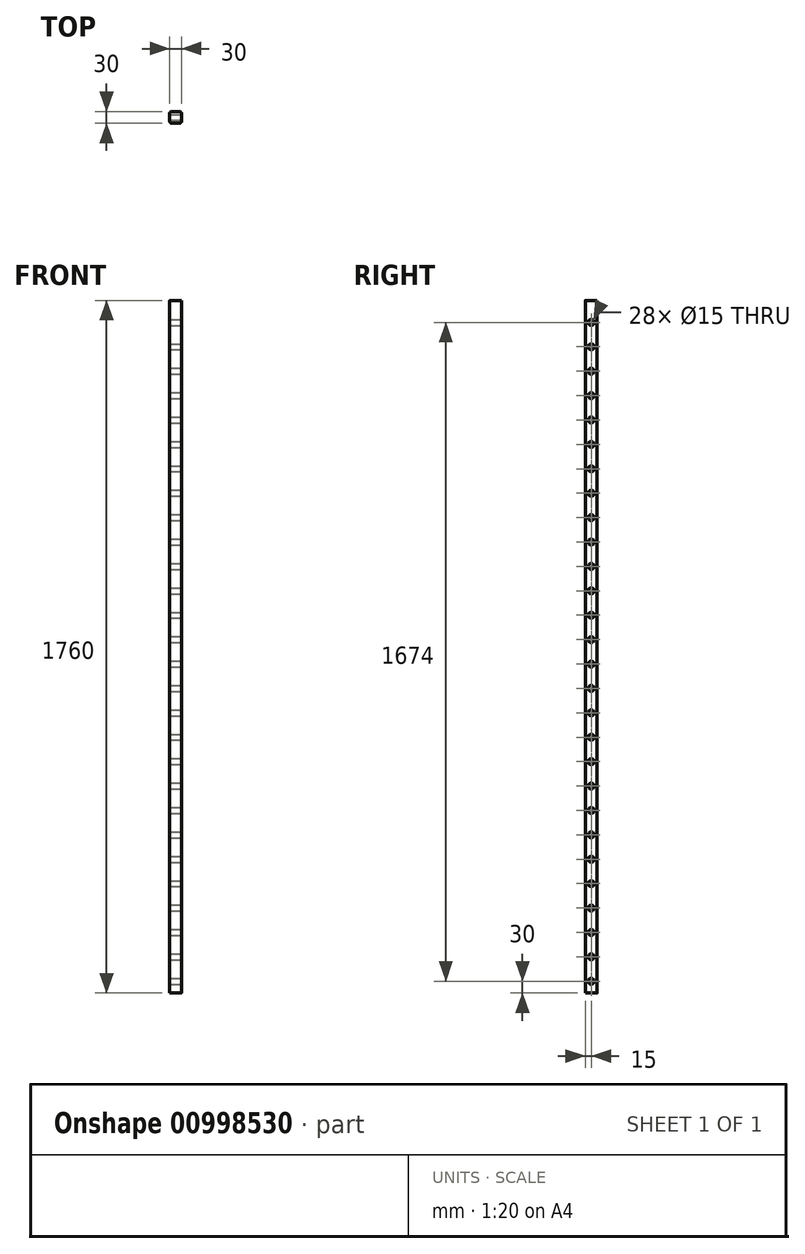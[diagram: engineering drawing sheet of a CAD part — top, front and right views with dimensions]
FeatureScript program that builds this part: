
annotation { "Feature Type Name" : "Feature", "Feature Type Description" : "" }
export const myFeature = defineFeature(function(context is Context, id is Id, definition is map)
    precondition{}
    {
        {
            var Q0;
            Q0=qCreatedBy(makeId("Top.planeOp"),FACE);
            var sketch = newSketch(context, id + "F0", { "sketchPlane" : qUnion([Q0])});
            skLineSegment(sketch, "E0.bottom", {"start": v(15, -15) * mm, "end": v(-15, -15) * mm});
            skLineSegment(sketch, "E0.top", {"start": v(15, 15) * mm, "end": v(-15, 15) * mm});
            skLineSegment(sketch, "E0.left", {"start": v(15, -15) * mm, "end": v(15, 15) * mm});
            skLineSegment(sketch, "E0.right", {"start": v(-15, -15) * mm, "end": v(-15, 15) * mm});
            skPoint(sketch, "E0.middle", {"position": v(0, 0) * mm});
            skSolve(sketch);
        }
        {
            var Q0;
            Q0 = qSketchRegion(id + "F0", true);
            extrude(context, id + "F1", {"entities" : qUnion([Q0]), "depth" : 1760 * mm, "offsetDistance" : 25 * mm});
        }
        {
            var Q0;
            Q0=makeQuery(id+"F1.opExtrude","SWEPT_FACE",FACE,{"disambiguationData":[OSD([sQuery(id+"F0.wireOp",EDGE,"E0.left")])]});
            var sketch = newSketch(context, id + "F2", { "sketchPlane" : qUnion([Q0])});
            skCircle(sketch, "E1", {"center": v(0, 30) * mm, "radius": 7.5 * mm});
            skCircle(sketch, "E2.0.1.0", {"center": v(0, 92) * mm, "radius": 7.5 * mm});
            skCircle(sketch, "E2.0.2.0", {"center": v(0, 154) * mm, "radius": 7.5 * mm});
            skCircle(sketch, "E2.0.3.0", {"center": v(0, 216) * mm, "radius": 7.5 * mm});
            skCircle(sketch, "E2.0.4.0", {"center": v(0, 278) * mm, "radius": 7.5 * mm});
            skCircle(sketch, "E2.0.5.0", {"center": v(0, 340) * mm, "radius": 7.5 * mm});
            skCircle(sketch, "E2.0.6.0", {"center": v(0, 402) * mm, "radius": 7.5 * mm});
            skCircle(sketch, "E2.0.7.0", {"center": v(0, 464) * mm, "radius": 7.5 * mm});
            skCircle(sketch, "E2.0.8.0", {"center": v(0, 526) * mm, "radius": 7.5 * mm});
            skCircle(sketch, "E2.0.9.0", {"center": v(0, 588) * mm, "radius": 7.5 * mm});
            skCircle(sketch, "E2.0.10.0", {"center": v(0, 650) * mm, "radius": 7.5 * mm});
            skCircle(sketch, "E2.0.11.0", {"center": v(0, 712) * mm, "radius": 7.5 * mm});
            skCircle(sketch, "E2.0.12.0", {"center": v(0, 774) * mm, "radius": 7.5 * mm});
            skCircle(sketch, "E2.0.13.0", {"center": v(0, 836) * mm, "radius": 7.5 * mm});
            skCircle(sketch, "E2.0.14.0", {"center": v(0, 898) * mm, "radius": 7.5 * mm});
            skCircle(sketch, "E2.0.15.0", {"center": v(0, 960) * mm, "radius": 7.5 * mm});
            skCircle(sketch, "E2.0.16.0", {"center": v(0, 1022) * mm, "radius": 7.5 * mm});
            skCircle(sketch, "E2.0.17.0", {"center": v(0, 1084) * mm, "radius": 7.5 * mm});
            skCircle(sketch, "E2.0.18.0", {"center": v(0, 1146) * mm, "radius": 7.5 * mm});
            skCircle(sketch, "E2.0.19.0", {"center": v(0, 1208) * mm, "radius": 7.5 * mm});
            skCircle(sketch, "E2.0.20.0", {"center": v(0, 1270) * mm, "radius": 7.5 * mm});
            skCircle(sketch, "E2.0.21.0", {"center": v(0, 1332) * mm, "radius": 7.5 * mm});
            skCircle(sketch, "E2.0.22.0", {"center": v(0, 1394) * mm, "radius": 7.5 * mm});
            skCircle(sketch, "E2.0.23.0", {"center": v(0, 1456) * mm, "radius": 7.5 * mm});
            skCircle(sketch, "E2.0.24.0", {"center": v(0, 1518) * mm, "radius": 7.5 * mm});
            skCircle(sketch, "E2.0.25.0", {"center": v(0, 1580) * mm, "radius": 7.5 * mm});
            skCircle(sketch, "E2.0.26.0", {"center": v(0, 1642) * mm, "radius": 7.5 * mm});
            skCircle(sketch, "E2.0.27.0", {"center": v(0, 1704) * mm, "radius": 7.5 * mm});
            skLineSegment(sketch, "E2.direction1", {"start": v(0, 30) * mm, "end": v(25, 30) * mm, "construction": true});
            skLineSegment(sketch, "E2.direction2", {"start": v(0, 30) * mm, "end": v(0, 92) * mm, "construction": true});
            skSolve(sketch);
        }
        {
            var Q0;
            Q0 = qSketchRegion(id + "F2", true);
            extrude(context, id + "F3", {"entities" : qUnion([Q0]), "operationType" : NewBodyOperationType.REMOVE, "endBound" : BoundingType.THROUGH_ALL, "oppositeDirection" : true, "depth" : 25 * mm, "offsetDistance" : 25 * mm});
        }
        {
            var Q0;
            Q0=makeQuery(id+"F1.opExtrude","SWEPT_EDGE",EDGE,{"disambiguationData":[OSD([sQuery(id+"F0.wireOp",EDGE,"E0.bottom"),sQuery(id+"F0.wireOp",EDGE,"E0.left")])]});
            var Q1;
            Q1=makeQuery(id+"F1.opExtrude","SWEPT_EDGE",EDGE,{"disambiguationData":[OSD([sQuery(id+"F0.wireOp",EDGE,"E0.bottom"),sQuery(id+"F0.wireOp",EDGE,"E0.right")])]});
            var Q2;
            Q2=makeQuery(id+"F1.opExtrude","SWEPT_EDGE",EDGE,{"disambiguationData":[OSD([sQuery(id+"F0.wireOp",EDGE,"E0.top"),sQuery(id+"F0.wireOp",EDGE,"E0.left")])]});
            var Q3;
            Q3=makeQuery(id+"F1.opExtrude","SWEPT_EDGE",EDGE,{"disambiguationData":[OSD([sQuery(id+"F0.wireOp",EDGE,"E0.top"),sQuery(id+"F0.wireOp",EDGE,"E0.right")])]});
            fillet(context, id + "F4", {"entities" : qUnion([Q0, Q1, Q2, Q3]), "radius" : 5 * mm, "tangentPropagation" : true, "allowEdgeOverflow" : false});
        }
    });
